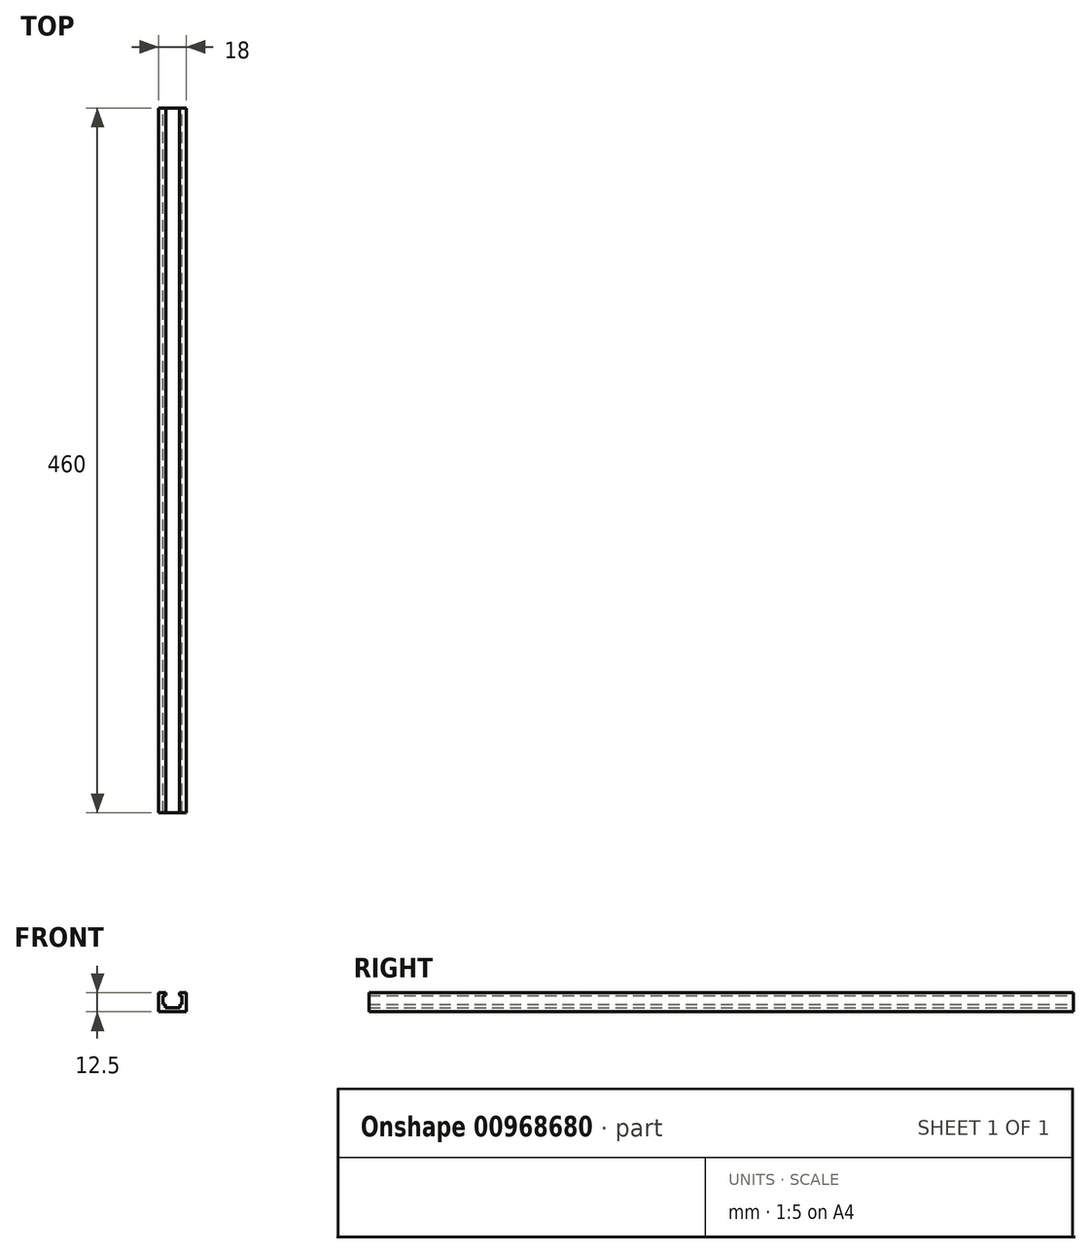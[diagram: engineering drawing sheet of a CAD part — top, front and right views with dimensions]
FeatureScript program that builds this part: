
annotation { "Feature Type Name" : "Feature", "Feature Type Description" : "" }
export const myFeature = defineFeature(function(context is Context, id is Id, definition is map)
    precondition{}
    {
        {
            var Q0;
            Q0=qCreatedBy(makeId("Front.planeOp"),FACE);
            var sketch = newSketch(context, id + "F0", { "sketchPlane" : qUnion([Q0])});
            skLineSegment(sketch, "E0", {"start": v(0, 0) * mm, "end": v(-9, 0) * mm});
            skLineSegment(sketch, "E1", {"start": v(-9, 0) * mm, "end": v(-9, 12.5) * mm});
            skLineSegment(sketch, "E2", {"start": v(-9, 12.5) * mm, "end": v(-4.5, 12.5) * mm});
            skLineSegment(sketch, "E3", {"start": v(-4.5, 12.5) * mm, "end": v(-4.5, 10.5) * mm});
            skLineSegment(sketch, "E4", {"start": v(-4.5, 10.5) * mm, "end": v(-6.25, 10.5) * mm});
            skLineSegment(sketch, "E5", {"start": v(-6.25, 10.5) * mm, "end": v(-6.25, 5) * mm});
            skLineSegment(sketch, "E6", {"start": v(-6.25, 5) * mm, "end": v(-4.75, 5) * mm});
            skLineSegment(sketch, "E7", {"start": v(-4.75, 5) * mm, "end": v(-4.75, 2.5) * mm});
            skLineSegment(sketch, "E8", {"start": v(-4.75, 2.5) * mm, "end": v(0, 2.5) * mm});
            skLineSegment(sketch, "E9", {"start": v(0, 2.5) * mm, "end": v(0, 0) * mm, "construction": true});
            skLineSegment(sketch, "E10.MirrorCS", {"start": v(6.25, 5) * mm, "end": v(4.75, 5) * mm});
            skLineSegment(sketch, "E11.MirrorCS", {"start": v(4.5, 10.5) * mm, "end": v(6.25, 10.5) * mm});
            skLineSegment(sketch, "E12.MirrorCS", {"start": v(9, 12.5) * mm, "end": v(4.5, 12.5) * mm});
            skLineSegment(sketch, "E13.MirrorCS", {"start": v(4.5, 12.5) * mm, "end": v(4.5, 10.5) * mm});
            skLineSegment(sketch, "E14.MirrorCS", {"start": v(9, 0) * mm, "end": v(9, 12.5) * mm});
            skLineSegment(sketch, "E15.MirrorCS", {"start": v(6.25, 10.5) * mm, "end": v(6.25, 5) * mm});
            skLineSegment(sketch, "E16.MirrorCS", {"start": v(4.75, 5) * mm, "end": v(4.75, 2.5) * mm});
            skLineSegment(sketch, "E17.MirrorCS", {"start": v(0, 0) * mm, "end": v(9, 0) * mm});
            skLineSegment(sketch, "E18.MirrorCS", {"start": v(4.75, 2.5) * mm, "end": v(0, 2.5) * mm});
            skSolve(sketch);
        }
        {
            var Q0;
            Q0=makeQuery(id+"F0.imprint","IMPRINT",FACE,{"disambiguationData":[TD([[makeQuery(id+"F0.imprint","IMPRINT",EDGE,{"derivedFrom":sQuery(id+"F0.wireOp",EDGE,"E0")}),-1.0]])]});
            extrude(context, id + "F1", {"entities" : qUnion([Q0]), "endBound" : BoundingType.SYMMETRIC, "depth" : 460 * mm, "offsetDistance" : 25 * mm});
        }
    });
